# Revit family: LBUL-20
name_source: partatom
category: Lighting Fixtures
revit_build: Autodesk Revit 2014 (Build: 20130308_1515(x64)
units: mm (PartAtom-declared; Revit-internal decimal feet)

## types (3) — shared parameters
Apparent Load = 20 VA
Assembly Code = D5020200
Certifications = Fixture is certified for use in wet locations
Color Filter = 16777215
Colt = Bullet : Colt
Connector Description = Lighting Connector
Default Elevation = 48 "
Description = Colt Bullet
Dimming Lamp Color Temperature Shift = <None>
Features = • Traditional landscape
form with improved
performance and efficacy
• 1/2 inch x 14 NPS mount
and adjustable knuckle
for aiming
• Wide NEMA 6x6
distribution provides
uniform lighting on
surface
Housing Material = Paint - Hubbell - Metallic Bronze Textured
Lamp = LED
Load Classification = Lighting
Manufacturer = Hubbell Outdoor Lighting
Model = LBUL-20-120-3K
Power Factor = 1
Reflector Finish = Hubbell - White Glass
Tilt Angle = 180.00°
URL = https://www.hubbell.com
Voltage = 120 V
Warranty = 5 years Warranty
Wattage Comments = 20W
Watts = 20 W

## per-type parameters (varying)
| type | LBUL | MBUL | Photometric Web File |
| LBUL-20-120-3K | Yes | No | LBUL-20-120-3K.ies |
| MBUL-1L3K-1 | No | Yes | LBUL-20-120-3K.ies |
| LBUL-20-120-4K | Yes | No | LBUL-20-120-4K.ies |

## geometry (parser evidence)
native form markers: Sweep x6
no freeform markers — native parametric forms only
